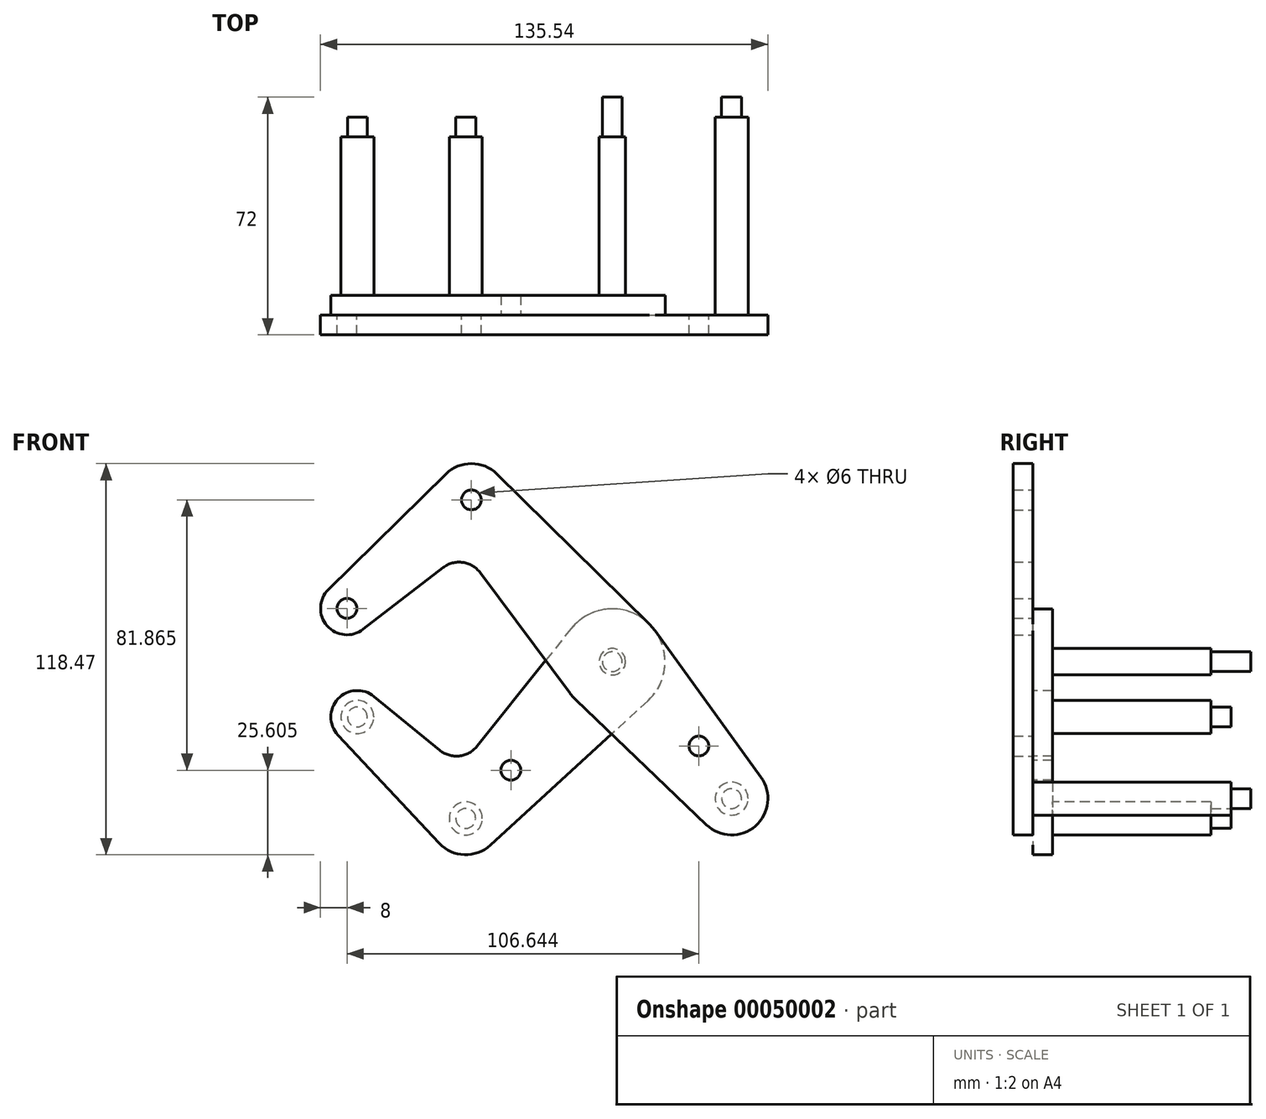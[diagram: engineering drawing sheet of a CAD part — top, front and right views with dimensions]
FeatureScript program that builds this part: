
annotation { "Feature Type Name" : "Feature", "Feature Type Description" : "" }
export const myFeature = defineFeature(function(context is Context, id is Id, definition is map)
    precondition{}
    {
        {
            var Q0;
            Q0=qCreatedBy(makeId("Front.planeOp"),FACE);
            cPlane(context, id + "F0", {"entities" : qUnion([Q0]), "cplaneType" : CPlaneType.OFFSET, "offset" : 30 * mm, "width" : 150 * mm, "height" : 150 * mm});
        }
        {
            var Q0;
            Q0=qCreatedBy(id+"F0.planeOp",FACE);
            var sketch = newSketch(context, id + "F1", { "sketchPlane" : qUnion([Q0])});
            skLineSegment(sketch, "E0", {"start": v(-42.7, 49) * mm, "end": v(36.14, -41.46) * mm, "construction": true});
            skCircle(sketch, "E1", {"center": v(0, 0) * mm, "radius": 3 * mm});
            skCircle(sketch, "E2", {"center": v(36.14, -41.46) * mm, "radius": 3 * mm});
            skCircle(sketch, "E3", {"center": v(-42.7, 49) * mm, "radius": 3 * mm});
            skCircle(sketch, "E4", {"center": v(-80.4, 16.15) * mm, "radius": 3 * mm});
            skLineSegment(sketch, "E5", {"start": v(-42.7, 49) * mm, "end": v(-80.4, 16.15) * mm, "construction": true});
            skCircle(sketch, "E6", {"center": v(36.14, -41.46) * mm, "radius": 11 * mm});
            skCircle(sketch, "E7", {"center": v(-80.4, 16.15) * mm, "radius": 8 * mm});
            skCircle(sketch, "E8", {"center": v(-42.7, 49) * mm, "radius": 11 * mm});
            skLineSegment(sketch, "E9", {"start": v(-86, 21.85) * mm, "end": v(-50.42, 56.84) * mm});
            skLineSegment(sketch, "E10", {"start": v(-75.52, 9.81) * mm, "end": v(-51.3, 28.49) * mm});
            skCircle(sketch, "E11", {"center": v(0, 0) * mm, "radius": 16 * mm});
            skLineSegment(sketch, "E12", {"start": v(-35, 56.84) * mm, "end": v(11.22, 11.4) * mm});
            skLineSegment(sketch, "E13", {"start": v(-40, 26.93) * mm, "end": v(-12.83, -9.55) * mm});
            skLineSegment(sketch, "E14", {"start": v(-11.06, -11.57) * mm, "end": v(28.54, -49.41) * mm});
            skLineSegment(sketch, "E15", {"start": v(12.97, 9.37) * mm, "end": v(45.05, -35.02) * mm});
            skArc(sketch, "E16.filletArc", {"start": v(-40, 26.93) * mm, "mid": v(-45.32, 30.08) * mm, "end": v(-51.3, 28.49) * mm});
            skLineSegment(sketch, "E17", {"start": v(0, 0) * mm, "end": v(-44.4, -47.47) * mm, "construction": true});
            skLineSegment(sketch, "E18", {"start": v(-44.4, -47.47) * mm, "end": v(-77.27, -16.73) * mm, "construction": true});
            skCircle(sketch, "E19", {"center": v(-77.27, -16.73) * mm, "radius": 3 * mm});
            skCircle(sketch, "E20", {"center": v(-44.4, -47.47) * mm, "radius": 3 * mm});
            skCircle(sketch, "E21", {"center": v(-77.27, -16.73) * mm, "radius": 8 * mm});
            skCircle(sketch, "E22", {"center": v(-44.4, -47.47) * mm, "radius": 11 * mm});
            skLineSegment(sketch, "E23", {"start": v(-72.2, -10.54) * mm, "end": v(-52.3, -26.8) * mm});
            skLineSegment(sketch, "E24", {"start": v(-83.1, -22.2) * mm, "end": v(-52.43, -54.99) * mm});
            skLineSegment(sketch, "E25", {"start": v(-12.5, 10) * mm, "end": v(-41, -25.61) * mm});
            skLineSegment(sketch, "E26", {"start": v(10.8, -11.8) * mm, "end": v(-36.97, -55.58) * mm});
            skArc(sketch, "E27.filletArc", {"start": v(-52.3, -26.8) * mm, "mid": v(-46.4, -28.57) * mm, "end": v(-41, -25.61) * mm});
            skCircle(sketch, "E28", {"center": v(-30.74, -32.86) * mm, "radius": 3 * mm});
            skCircle(sketch, "E29", {"center": v(26.24, -25.54) * mm, "radius": 3 * mm});
            skLineSegment(sketch, "E30", {"start": v(26.24, -25.54) * mm, "end": v(23.98, -27.52) * mm, "construction": true});
            skCircle(sketch, "E31", {"center": v(0, 0) * mm, "radius": 4 * mm});
            skCircle(sketch, "E32", {"center": v(-80.4, 16.15) * mm, "radius": 5 * mm});
            skCircle(sketch, "E33", {"center": v(-77.27, -16.73) * mm, "radius": 5 * mm});
            skCircle(sketch, "E34", {"center": v(36.14, -41.46) * mm, "radius": 5 * mm});
            skCircle(sketch, "E35", {"center": v(-44.4, -47.47) * mm, "radius": 5 * mm});
            skSolve(sketch);
        }
        {
            var Q0;
            Q0=makeQuery(id+"F1.imprint","IMPRINT",FACE,{"disambiguationData":[TD([[makeQuery(id+"F1.imprint","IMPRINT",EDGE,{"derivedFrom":sQuery(id+"F1.wireOp",EDGE,"E32")}),-1.0]])]});
            var Q1;
            Q1=makeQuery(id+"F1.imprint","IMPRINT",FACE,{"disambiguationData":[TD([[makeQuery(id+"F1.imprint","IMPRINT",EDGE,{"derivedFrom":sQuery(id+"F1.wireOp",EDGE,"E4")}),-1.0]])]});
            var Q2;
            {var subQ9=sQuery(id+"F1.wireOp",EDGE,"E9");Q2=makeQuery(id+"F1.imprint","IMPRINT",FACE,{"disambiguationData":[TD([[makeQuery(id+"F1.imprint","IMPRINT",EDGE,{"derivedFrom":subQ9}),-1.0]])]});}
            var Q3;
            Q3=makeQuery(id+"F1.imprint","IMPRINT",FACE,{"disambiguationData":[TD([[makeQuery(id+"F1.imprint","IMPRINT",EDGE,{"derivedFrom":sQuery(id+"F1.wireOp",EDGE,"E3")}),-1.0]])]});
            var Q4;
            Q4=makeQuery(id+"F1.imprint","IMPRINT",FACE,{"disambiguationData":[TD([[makeQuery(id+"F1.imprint","IMPRINT",EDGE,{"derivedFrom":sQuery(id+"F1.wireOp",EDGE,"E31")}),-1.0]])]});
            var Q5;
            {var subQ1=sQuery(id+"F1.wireOp",EDGE,"E13");var subQ3=sQuery(id+"F1.wireOp",EDGE,"E11");var subQ5=makeQuery(id+"F1.imprint","INTERSECT",VERTEX,{"derivedFrom":[subQ3,subQ1]});Q5=makeQuery(id+"F1.imprint","IMPRINT",FACE,{"disambiguationData":[TD([[makeQuery(id+"F1.imprint","IMPRINT",EDGE,{"disambiguationData":[TD([[subQ5,1.0]])],"derivedFrom":subQ3}),-1.0]])]});}
            var Q6;
            Q6=makeQuery(id+"F1.imprint","IMPRINT",FACE,{"disambiguationData":[TD([[makeQuery(id+"F1.imprint","IMPRINT",EDGE,{"derivedFrom":sQuery(id+"F1.wireOp",EDGE,"E1")}),-1.0]])]});
            var Q7;
            {var subQ1=sQuery(id+"F1.wireOp",EDGE,"E15");Q7=makeQuery(id+"F1.imprint","IMPRINT",FACE,{"disambiguationData":[TD([[makeQuery(id+"F1.imprint","IMPRINT",EDGE,{"derivedFrom":subQ1}),-1.0]])]});}
            var Q8;
            Q8=makeQuery(id+"F1.imprint","IMPRINT",FACE,{"disambiguationData":[TD([[makeQuery(id+"F1.imprint","IMPRINT",EDGE,{"derivedFrom":sQuery(id+"F1.wireOp",EDGE,"E34")}),-1.0]])]});
            var Q9;
            Q9=makeQuery(id+"F1.imprint","IMPRINT",FACE,{"disambiguationData":[TD([[makeQuery(id+"F1.imprint","IMPRINT",EDGE,{"derivedFrom":sQuery(id+"F1.wireOp",EDGE,"E2")}),-1.0]])]});
            var Q10;
            {var subQ1=sQuery(id+"F1.wireOp",EDGE,"E14");var subQ3=sQuery(id+"F1.wireOp",EDGE,"E11");var subQ5=makeQuery(id+"F1.imprint","INTERSECT",VERTEX,{"derivedFrom":[subQ3,subQ1]});Q10=makeQuery(id+"F1.imprint","IMPRINT",FACE,{"disambiguationData":[TD([[makeQuery(id+"F1.imprint","IMPRINT",EDGE,{"disambiguationData":[TD([[subQ5,-1.0]])],"derivedFrom":subQ3}),-1.0]])]});}
            extrude(context, id + "F2", {"entities" : qUnion([Q0, Q1, Q2, Q3, Q4, Q5, Q6, Q7, Q8, Q9, Q10]), "depth" : 6 * mm});
        }
        {
            var Q0;
            Q0=makeQuery(id+"F1.imprint","IMPRINT",FACE,{"disambiguationData":[TD([[makeQuery(id+"F1.imprint","IMPRINT",EDGE,{"derivedFrom":sQuery(id+"F1.wireOp",EDGE,"E33")}),-1.0]])]});
            var Q1;
            Q1=makeQuery(id+"F1.imprint","IMPRINT",FACE,{"disambiguationData":[TD([[makeQuery(id+"F1.imprint","IMPRINT",EDGE,{"derivedFrom":sQuery(id+"F1.wireOp",EDGE,"E19")}),-1.0]])]});
            var Q2;
            {var subQ2=sQuery(id+"F1.wireOp",EDGE,"E23");Q2=makeQuery(id+"F1.imprint","IMPRINT",FACE,{"disambiguationData":[TD([[makeQuery(id+"F1.imprint","IMPRINT",EDGE,{"derivedFrom":subQ2}),-1.0]])]});}
            var Q3;
            Q3=makeQuery(id+"F1.imprint","IMPRINT",FACE,{"disambiguationData":[TD([[makeQuery(id+"F1.imprint","IMPRINT",EDGE,{"derivedFrom":sQuery(id+"F1.wireOp",EDGE,"E35")}),-1.0]])]});
            var Q4;
            Q4=makeQuery(id+"F1.imprint","IMPRINT",FACE,{"disambiguationData":[TD([[makeQuery(id+"F1.imprint","IMPRINT",EDGE,{"derivedFrom":sQuery(id+"F1.wireOp",EDGE,"E20")}),-1.0]])]});
            var Q5;
            {var subQ1=sQuery(id+"F1.wireOp",EDGE,"E14");var subQ3=sQuery(id+"F1.wireOp",EDGE,"E11");var subQ5=makeQuery(id+"F1.imprint","INTERSECT",VERTEX,{"derivedFrom":[subQ3,subQ1]});Q5=makeQuery(id+"F1.imprint","IMPRINT",FACE,{"disambiguationData":[TD([[makeQuery(id+"F1.imprint","IMPRINT",EDGE,{"disambiguationData":[TD([[subQ5,-1.0]])],"derivedFrom":subQ3}),-1.0]])]});}
            var Q6;
            {var subQ1=sQuery(id+"F1.wireOp",EDGE,"E13");var subQ3=sQuery(id+"F1.wireOp",EDGE,"E11");var subQ5=makeQuery(id+"F1.imprint","INTERSECT",VERTEX,{"derivedFrom":[subQ3,subQ1]});Q6=makeQuery(id+"F1.imprint","IMPRINT",FACE,{"disambiguationData":[TD([[makeQuery(id+"F1.imprint","IMPRINT",EDGE,{"disambiguationData":[TD([[subQ5,1.0]])],"derivedFrom":subQ3}),-1.0]])]});}
            var Q7;
            Q7=makeQuery(id+"F1.imprint","IMPRINT",FACE,{"disambiguationData":[TD([[makeQuery(id+"F1.imprint","IMPRINT",EDGE,{"derivedFrom":sQuery(id+"F1.wireOp",EDGE,"E31")}),-1.0]])]});
            var Q8;
            Q8=makeQuery(id+"F1.imprint","IMPRINT",FACE,{"disambiguationData":[TD([[makeQuery(id+"F1.imprint","IMPRINT",EDGE,{"derivedFrom":sQuery(id+"F1.wireOp",EDGE,"E1")}),-1.0]])]});
            extrude(context, id + "F3", {"entities" : qUnion([Q0, Q1, Q2, Q3, Q4, Q5, Q6, Q7, Q8]), "oppositeDirection" : true, "depth" : 6 * mm});
        }
        {
            var Q0;
            Q0=makeQuery(id+"F1.imprint","IMPRINT",FACE,{"disambiguationData":[TD([[makeQuery(id+"F1.imprint","IMPRINT",EDGE,{"derivedFrom":sQuery(id+"F1.wireOp",EDGE,"E2")}),1.0]])]});
            var Q1;
            Q1=makeQuery(id+"F1.imprint","IMPRINT",FACE,{"disambiguationData":[TD([[makeQuery(id+"F1.imprint","IMPRINT",EDGE,{"derivedFrom":sQuery(id+"F1.wireOp",EDGE,"E2")}),-1.0]])]});
            var Q2;
            Q2=makeQuery(id+"F1.imprint","IMPRINT",FACE,{"disambiguationData":[TD([[makeQuery(id+"F1.imprint","IMPRINT",EDGE,{"derivedFrom":sQuery(id+"F1.wireOp",EDGE,"E1")}),1.0]])]});
            var Q3;
            Q3=makeQuery(id+"F1.imprint","IMPRINT",FACE,{"disambiguationData":[TD([[makeQuery(id+"F1.imprint","IMPRINT",EDGE,{"derivedFrom":sQuery(id+"F1.wireOp",EDGE,"E1")}),-1.0]])]});
            var Q4;
            Q4=qCreatedBy(makeId("Front.planeOp"),FACE);
            var Q5;
            Q5=makeQuery(id+"F2.opExtrude","CAP_FACE",FACE,{"disambiguationData":[OSD([sQuery(id+"F1.wireOp",EDGE,"E1"),sQuery(id+"F1.wireOp",EDGE,"E2"),sQuery(id+"F1.wireOp",EDGE,"E3"),sQuery(id+"F1.wireOp",EDGE,"E4"),sQuery(id+"F1.wireOp",EDGE,"E6"),sQuery(id+"F1.wireOp",EDGE,"E7"),sQuery(id+"F1.wireOp",EDGE,"E8"),sQuery(id+"F1.wireOp",EDGE,"E9"),sQuery(id+"F1.wireOp",EDGE,"E10"),sQuery(id+"F1.wireOp",EDGE,"E11"),sQuery(id+"F1.wireOp",EDGE,"E12"),sQuery(id+"F1.wireOp",EDGE,"E13"),sQuery(id+"F1.wireOp",EDGE,"E14"),sQuery(id+"F1.wireOp",EDGE,"E15"),sQuery(id+"F1.wireOp",EDGE,"E16.filletArc"),sQuery(id+"F1.wireOp",EDGE,"E29")])],"isStart":false});
            extrude(context, id + "F4", {"entities" : qUnion([Q0, Q1, Q2, Q3]), "endBound" : BoundingType.UP_TO_SURFACE, "oppositeDirection" : true, "endBoundEntityFace" : qUnion([Q4]), "depth" : 25 * mm, "hasSecondDirection" : true, "secondDirectionBound" : SecondDirectionBoundingType.UP_TO_SURFACE, "secondDirectionOppositeDirection" : false, "secondDirectionBoundEntityFace" : qUnion([Q5]), "secondDirectionDepth" : 25 * mm});
        }
        {
            var Q0;
            Q0=makeQuery(id+"F1.imprint","IMPRINT",FACE,{"disambiguationData":[TD([[makeQuery(id+"F1.imprint","IMPRINT",EDGE,{"derivedFrom":sQuery(id+"F1.wireOp",EDGE,"E19")}),1.0]])]});
            var Q1;
            Q1=makeQuery(id+"F1.imprint","IMPRINT",FACE,{"disambiguationData":[TD([[makeQuery(id+"F1.imprint","IMPRINT",EDGE,{"derivedFrom":sQuery(id+"F1.wireOp",EDGE,"E19")}),-1.0]])]});
            var Q2;
            Q2=makeQuery(id+"F1.imprint","IMPRINT",FACE,{"disambiguationData":[TD([[makeQuery(id+"F1.imprint","IMPRINT",EDGE,{"derivedFrom":sQuery(id+"F1.wireOp",EDGE,"E20")}),1.0]])]});
            var Q3;
            Q3=makeQuery(id+"F1.imprint","IMPRINT",FACE,{"disambiguationData":[TD([[makeQuery(id+"F1.imprint","IMPRINT",EDGE,{"derivedFrom":sQuery(id+"F1.wireOp",EDGE,"E20")}),-1.0]])]});
            var Q4;
            Q4=qCreatedBy(makeId("Front.planeOp"),FACE);
            extrude(context, id + "F5", {"entities" : qUnion([Q0, Q1, Q2, Q3]), "endBound" : BoundingType.UP_TO_SURFACE, "oppositeDirection" : true, "endBoundEntityFace" : qUnion([Q4]), "depth" : 25 * mm});
        }
        {
            var Q0;
            Q0=makeQuery(id+"F2.opExtrude","SWEPT_BODY",BODY,{"disambiguationData":[OSD([sQuery(id+"F1.wireOp",EDGE,"E1"),sQuery(id+"F1.wireOp",EDGE,"E2"),sQuery(id+"F1.wireOp",EDGE,"E3"),sQuery(id+"F1.wireOp",EDGE,"E4"),sQuery(id+"F1.wireOp",EDGE,"E6"),sQuery(id+"F1.wireOp",EDGE,"E7"),sQuery(id+"F1.wireOp",EDGE,"E8"),sQuery(id+"F1.wireOp",EDGE,"E9"),sQuery(id+"F1.wireOp",EDGE,"E10"),sQuery(id+"F1.wireOp",EDGE,"E11"),sQuery(id+"F1.wireOp",EDGE,"E12"),sQuery(id+"F1.wireOp",EDGE,"E13"),sQuery(id+"F1.wireOp",EDGE,"E14"),sQuery(id+"F1.wireOp",EDGE,"E15"),sQuery(id+"F1.wireOp",EDGE,"E16.filletArc"),sQuery(id+"F1.wireOp",EDGE,"E29")])]});
            var Q1;
            Q1=makeQuery(id+"F3.opExtrude","SWEPT_BODY",BODY,{"disambiguationData":[OSD([sQuery(id+"F1.wireOp",EDGE,"E1"),sQuery(id+"F1.wireOp",EDGE,"E11"),sQuery(id+"F1.wireOp",EDGE,"E19"),sQuery(id+"F1.wireOp",EDGE,"E20"),sQuery(id+"F1.wireOp",EDGE,"E21"),sQuery(id+"F1.wireOp",EDGE,"E22"),sQuery(id+"F1.wireOp",EDGE,"E23"),sQuery(id+"F1.wireOp",EDGE,"E24"),sQuery(id+"F1.wireOp",EDGE,"E25"),sQuery(id+"F1.wireOp",EDGE,"E26"),sQuery(id+"F1.wireOp",EDGE,"E27.filletArc"),sQuery(id+"F1.wireOp",EDGE,"E28")])]});
            var Q2;
            Q2=makeQuery(id+"F5.opExtrude","SWEPT_BODY",BODY,{"disambiguationData":[OSD([sQuery(id+"F1.wireOp",EDGE,"E33")])]});
            var Q3;
            Q3=makeQuery(id+"F4.opExtrude","SWEPT_BODY",BODY,{"disambiguationData":[OSD([sQuery(id+"F1.wireOp",EDGE,"E34")])]});
            var Q4;
            Q4=makeQuery(id+"F4.opExtrude","SWEPT_BODY",BODY,{"disambiguationData":[OSD([sQuery(id+"F1.wireOp",EDGE,"E31")])]});
            var Q5;
            Q5=makeQuery(id+"F5.opExtrude","SWEPT_BODY",BODY,{"disambiguationData":[OSD([sQuery(id+"F1.wireOp",EDGE,"E35")])]});
            booleanBodies(context, id + "F6", {"operationType" : BooleanOperationType.SUBTRACTION, "tools" : qUnion([Q0, Q1]), "targets" : qUnion([Q2, Q3, Q4, Q5]), "keepTools" : true});
        }
        {
            var Q0;
            Q0=makeQuery(id+"F5.opExtrude","SWEPT_BODY",BODY,{"disambiguationData":[OSD([sQuery(id+"F1.wireOp",EDGE,"E33")])]});
            var Q1;
            Q1=makeQuery(id+"F4.opExtrude","SWEPT_BODY",BODY,{"disambiguationData":[OSD([sQuery(id+"F1.wireOp",EDGE,"E31")])]});
            var Q2;
            Q2=makeQuery(id+"F5.opExtrude","SWEPT_BODY",BODY,{"disambiguationData":[OSD([sQuery(id+"F1.wireOp",EDGE,"E35")])]});
            var Q3;
            Q3=makeQuery(id+"F4.opExtrude","SWEPT_BODY",BODY,{"disambiguationData":[OSD([sQuery(id+"F1.wireOp",EDGE,"E34")])]});
            var Q4;
            Q4=qCreatedBy(makeId("Front.planeOp"),FACE);
            mirror(context, id + "F7", {"operationType" : NewBodyOperationType.ADD, "entities" : qUnion([Q0, Q1, Q2, Q3]), "mirrorPlane" : qUnion([Q4])});
        }
    });
